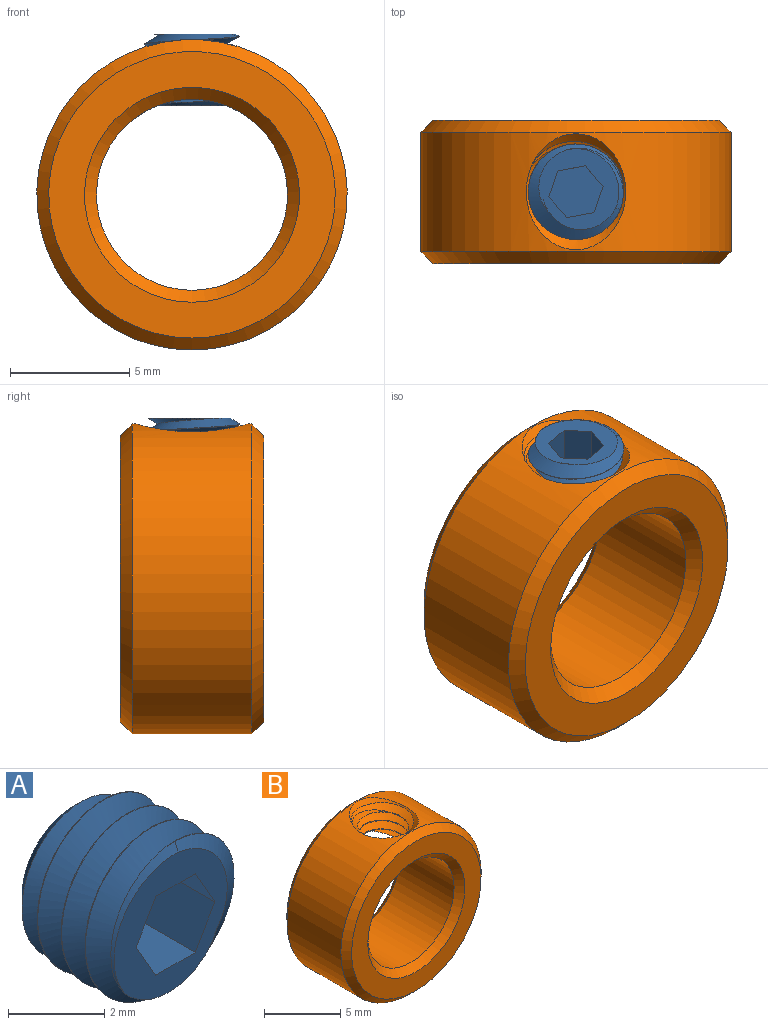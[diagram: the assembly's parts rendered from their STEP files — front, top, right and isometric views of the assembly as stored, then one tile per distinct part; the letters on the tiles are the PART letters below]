
ASSEMBLY  parts=2 mates=1
PART A: 14 faces, bbox 4.2x4x4.8 mm
  f0: plane 3.63x3.53mm, normal (0,-1,0), area 5.4mm2, adj f3,f5,f6,f7,f8,f9,f10,f11
  f1: cylinder r=2mm len=4mm, axis (0,1,0), area 0.7mm2, adj f3,f4,f5,f6
  f2: plane 3.02x3.02mm, normal (0,1,0), area 7mm2, adj f4,f5,f6
  f3: cone r=1.8mm half-angle=60deg, axis (0,1,0), area 0.5mm2, adj f0,f1,f5,f6
  f4: cone r=2mm half-angle=45deg, axis (0,-1,0), area 3.2mm2, adj f1,f2,f5,f6
  f5: bspline ~4.62x4mm, area 28.8mm2, adj f0,f1,f2,f3,f4,f6
  f6: bspline ~4.62x4mm, area 28.9mm2, adj f0,f1,f2,f3,f4,f5
  f7: plane 1.5x1mm, normal (0.87,0,-0.5), area 1.7mm2, adj f0,f8,f12,f13
  f8: plane 1.5x1mm, normal (0.87,0,0.5), area 1.7mm2, adj f0,f7,f9,f13
  f9: plane 1.5x1.15mm, normal (0,0,1), area 1.7mm2, adj f0,f8,f10,f13
  f10: plane 1.5x1mm, normal (-0.87,0,0.5), area 1.7mm2, adj f0,f9,f11,f13
  f11: plane 1.5x1mm, normal (-0.87,0,-0.5), area 1.7mm2, adj f0,f10,f12,f13
  f12: plane 1.5x1.15mm, normal (0,0,-1), area 1.7mm2, adj f0,f7,f11,f13
  f13: plane 2.31x2mm, normal (0,-1,0), area 3.5mm2, adj f7,f8,f9,f10,f11,f12
PART B: 13 faces, bbox 13x6x13.2 mm
  f0: cylinder r=1.62mm len=3.25mm, axis (0,0,-1), area 1.2mm2, adj f1,f9,f11,f12
  f1: cone r=2.43mm half-angle=45deg, axis (0,0,1), area 6.4mm2, adj f0,f2,f9,f12
  f2: cylinder r=6.5mm len=13mm, axis (0,1,0), area 188.2mm2, adj f1,f3,f6,f9,f12
  f3: cone r=6mm half-angle=45deg, axis (0,1,0), area 27.8mm2, adj f2,f4
  f4: plane 12x12mm, normal (0,-1,0), area 49.5mm2, adj f3,f5
  f5: cone r=4mm half-angle=45deg, axis (0,-1,0), area 18.9mm2, adj f4,f11
  f6: cone r=6.5mm half-angle=45deg, axis (0,-1,0), area 27.8mm2, adj f2,f7
  f7: plane 12x12mm, normal (0,1,0), area 49.5mm2, adj f6,f8
  f8: cone r=4.5mm half-angle=45deg, axis (0,1,0), area 18.9mm2, adj f7,f11
  f9: bspline ~5.07x4.39mm, area 25.3mm2, adj f0,f1,f2,f10,f11,f12
  f10: bspline ~2.16x0.4mm, area 0mm2, adj f9,f11
  f11: cylinder r=4mm len=8mm, axis (0,1,0), area 113.8mm2, adj f0,f5,f8,f9,f10,f12
  f12: bspline ~5.07x4.39mm, area 25mm2, adj f0,f1,f2,f9,f11
PLACE A rot(axis=(-0.45,0.63,-0.63),131.7deg) t=(0,0,5.23)mm
PLACE B at identity
MATE cylindrical A.f1 <-> B.f0  axis (0,0,1) through (0,0,6.73)mm
